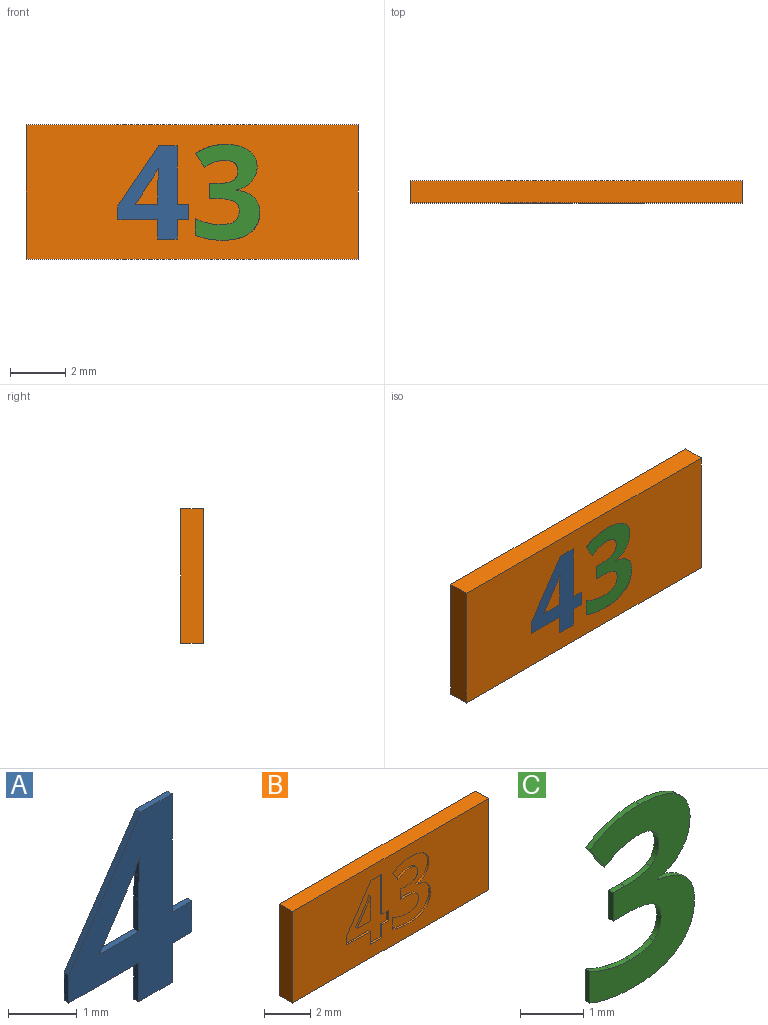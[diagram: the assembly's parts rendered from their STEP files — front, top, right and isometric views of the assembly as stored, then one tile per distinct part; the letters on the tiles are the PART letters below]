
ASSEMBLY  parts=3 mates=2
PART A: 20 faces, bbox 2.5x0.1x3.4 mm
  f0: plane 3.37x2.54mm, normal (0,-1,0), area 4.3mm2, adj f1,f2,f3,f4,f5,f6,f7,f8
  f1: plane 0.41x0.1mm, normal (0,0,1), area 0mm2, adj f0,f2,f13,f15
  f2: plane 2.12x0.1mm, normal (1,0,0), area 0.2mm2, adj f0,f1,f3,f13
  f3: plane 0.66x0.1mm, normal (0,0,1), area 0.1mm2, adj f0,f2,f4,f13
  f4: plane 2.18x1.48mm, normal (-0.83,0,0.56), area 0.3mm2, adj f0,f3,f5,f13
  f5: plane 0.5x0.1mm, normal (-1,0,0), area 0mm2, adj f0,f4,f6,f13
  f6: plane 1.44x0.1mm, normal (0,0,-1), area 0.1mm2, adj f0,f5,f7,f13
  f7: plane 0.7x0.1mm, normal (-1,0,0), area 0.1mm2, adj f0,f6,f8,f13
  f8: plane 0.7x0.1mm, normal (0,0,-1), area 0.1mm2, adj f0,f7,f13,f14
  f9: plane 0.93x0.62mm, normal (0.83,0,-0.55), area 0.1mm2, adj f0,f10,f13,f18
  f10: extruded ~0.37x0.21mm, area 0mm2, adj f0,f9,f11,f13
  f11: plane 0.1x0.02mm, normal (0,0,-1), area 0mm2, adj f0,f10,f12,f13
  f12: extruded ~0.32x0.1mm, area 0mm2, adj f0,f11,f13,f17
  f13: plane 3.37x2.54mm, normal (0,1,0), area 4.3mm2, adj f1,f2,f3,f4,f5,f6,f7,f8
  f14: plane 0.7x0.1mm, normal (1,0,0), area 0.1mm2, adj f0,f8,f13,f16
  f15: plane 0.55x0.1mm, normal (1,0,0), area 0.1mm2, adj f0,f1,f13,f16
  f16: plane 0.41x0.1mm, normal (0,0,-1), area 0mm2, adj f0,f13,f14,f15
  f17: extruded ~0.42x0.1mm, area 0mm2, adj f0,f12,f13,f19
  f18: plane 0.81x0.1mm, normal (0,0,1), area 0.1mm2, adj f0,f9,f13,f19
  f19: plane 0.57x0.1mm, normal (-1,0,0), area 0.1mm2, adj f0,f13,f17,f18
PART B: 54 faces, bbox 12x0.8x4.9 mm
  f0: plane 12x4.85mm, normal (0,-1,0), area 49.1mm2, adj f1,f2,f3,f4,f6,f7,f8,f9
  f1: plane 12x0.8mm, normal (0,0,-1), area 9.6mm2, adj f0,f2,f4,f5
  f2: plane 4.85x0.8mm, normal (1,0,0), area 3.9mm2, adj f0,f1,f3,f5
  f3: plane 12x0.8mm, normal (0,0,1), area 9.6mm2, adj f0,f2,f4,f5
  f4: plane 4.85x0.8mm, normal (-1,0,0), area 3.9mm2, adj f0,f1,f3,f5
  f5: plane 12x4.85mm, normal (0,1,0), area 58.2mm2, adj f1,f2,f3,f4
  f6: plane 0.55x0.1mm, normal (-1,0,0), area 0.1mm2, adj f0,f7,f23,f24
  f7: plane 0.41x0.1mm, normal (0,0,-1), area 0mm2, adj f0,f6,f8,f24
  f8: plane 2.12x0.1mm, normal (-1,0,0), area 0.2mm2, adj f0,f7,f9,f24
  f9: plane 0.66x0.1mm, normal (0,0,-1), area 0.1mm2, adj f0,f8,f10,f24
  f10: plane 2.18x1.48mm, normal (0.83,0,-0.56), area 0.3mm2, adj f0,f9,f11,f24
  f11: plane 0.5x0.1mm, normal (1,0,0), area 0mm2, adj f0,f10,f12,f24
  f12: plane 1.44x0.1mm, normal (0,0,1), area 0.1mm2, adj f0,f11,f13,f24
  f13: plane 0.7x0.1mm, normal (1,0,0), area 0.1mm2, adj f0,f12,f14,f24
  f14: plane 0.7x0.1mm, normal (0,0,1), area 0.1mm2, adj f0,f13,f15,f24
  f15: plane 0.7x0.1mm, normal (-1,0,0), area 0.1mm2, adj f0,f14,f23,f24
  f16: plane 0.81x0.1mm, normal (0,0,-1), area 0.1mm2, adj f17,f22,f24,f25
  f17: plane 0.93x0.62mm, normal (-0.83,0,0.55), area 0.1mm2, adj f16,f18,f24,f25
  f18: extruded ~0.37x0.21mm, area 0mm2, adj f17,f19,f24,f25
  f19: plane 0.1x0.02mm, normal (0,0,1), area 0mm2, adj f18,f20,f24,f25
  f20: extruded ~0.32x0.1mm, area 0mm2, adj f19,f21,f24,f25
  f21: extruded ~0.42x0.1mm, area 0mm2, adj f20,f22,f24,f25
  f22: plane 0.57x0.1mm, normal (1,0,0), area 0.1mm2, adj f16,f21,f24,f25
  f23: plane 0.41x0.1mm, normal (0,0,1), area 0mm2, adj f0,f6,f15,f24
  f24: plane 3.37x2.54mm, normal (0,-1,0), area 4.3mm2, adj f6,f7,f8,f9,f10,f11,f12,f13
  f25: plane 1.3x0.84mm, normal (0,-1,0), area 0.5mm2, adj f16,f17,f18,f19,f20,f21,f22
  f26: extruded ~0.59x0.3mm, area 0.1mm2, adj f0,f27,f52,f53
  f27: extruded ~0.83x0.21mm, area 0.1mm2, adj f0,f26,f28,f53
  f28: extruded ~1.1x0.33mm, area 0.1mm2, adj f0,f27,f29,f53
  f29: plane 0.49x0.33mm, normal (0.83,0,0.56), area 0.1mm2, adj f0,f28,f30,f53
  f30: extruded ~0.38x0.19mm, area 0mm2, adj f0,f29,f31,f53
  f31: extruded ~0.34x0.1mm, area 0mm2, adj f0,f30,f32,f53
  f32: extruded ~0.48x0.38mm, area 0.1mm2, adj f0,f31,f33,f53
  f33: extruded ~0.35x0.18mm, area 0mm2, adj f0,f32,f34,f53
  f34: extruded ~0.57x0.1mm, area 0.1mm2, adj f0,f33,f35,f53
  f35: plane 0.26x0.1mm, normal (0,0,-1), area 0mm2, adj f0,f34,f36,f53
  f36: plane 0.55x0.1mm, normal (1,0,0), area 0.1mm2, adj f0,f35,f37,f53
  f37: plane 0.26x0.1mm, normal (0,0,1), area 0mm2, adj f0,f36,f38,f53
  f38: extruded ~0.62x0.1mm, area 0.1mm2, adj f0,f37,f39,f53
  f39: extruded ~0.34x0.19mm, area 0mm2, adj f0,f38,f40,f53
  f40: extruded ~0.39x0.17mm, area 0mm2, adj f0,f39,f41,f53
  f41: extruded ~0.52x0.12mm, area 0.1mm2, adj f0,f40,f42,f53
  f42: extruded ~0.47x0.1mm, area 0mm2, adj f0,f41,f43,f53
  f43: extruded ~0.43x0.16mm, area 0mm2, adj f0,f42,f44,f53
  f44: plane 0.61x0.1mm, normal (1,0,0), area 0.1mm2, adj f0,f43,f45,f53
  f45: extruded ~0.97x0.18mm, area 0.1mm2, adj f0,f44,f46,f53
  f46: extruded ~1.01x0.27mm, area 0.1mm2, adj f0,f45,f47,f53
  f47: extruded ~0.76x0.35mm, area 0.1mm2, adj f0,f46,f48,f53
  f48: extruded ~0.53x0.21mm, area 0.1mm2, adj f0,f47,f49,f53
  f49: extruded ~0.62x0.25mm, area 0.1mm2, adj f0,f48,f50,f53
  f50: plane 0.1x0.01mm, normal (-1,0,0), area 0mm2, adj f0,f49,f51,f53
  f51: extruded ~0.54x0.3mm, area 0.1mm2, adj f0,f50,f52,f53
  f52: extruded ~0.54x0.19mm, area 0.1mm2, adj f0,f26,f51,f53
  f53: plane 3.47x2.33mm, normal (0,-1,0), area 4.3mm2, adj f26,f27,f28,f29,f30,f31,f32,f33
PART C: 29 faces, bbox 2.3x0.1x3.5 mm
  f0: plane 3.47x2.33mm, normal (0,-1,0), area 4.3mm2, adj f1,f2,f3,f4,f5,f6,f7,f8
  f1: extruded ~0.83x0.21mm, area 0.1mm2, adj f0,f2,f25,f27
  f2: extruded ~1.1x0.33mm, area 0.1mm2, adj f0,f1,f3,f25
  f3: plane 0.49x0.33mm, normal (-0.83,0,-0.56), area 0.1mm2, adj f0,f2,f4,f25
  f4: extruded ~0.38x0.19mm, area 0mm2, adj f0,f3,f5,f25
  f5: extruded ~0.34x0.1mm, area 0mm2, adj f0,f4,f6,f25
  f6: extruded ~0.48x0.38mm, area 0.1mm2, adj f0,f5,f7,f25
  f7: extruded ~0.35x0.18mm, area 0mm2, adj f0,f6,f8,f25
  f8: extruded ~0.57x0.1mm, area 0.1mm2, adj f0,f7,f9,f25
  f9: plane 0.26x0.1mm, normal (0,0,1), area 0mm2, adj f0,f8,f10,f25
  f10: plane 0.55x0.1mm, normal (-1,0,0), area 0.1mm2, adj f0,f9,f11,f25
  f11: plane 0.26x0.1mm, normal (0,0,-1), area 0mm2, adj f0,f10,f12,f25
  f12: extruded ~0.62x0.1mm, area 0.1mm2, adj f0,f11,f13,f25
  f13: extruded ~0.34x0.19mm, area 0mm2, adj f0,f12,f14,f25
  f14: extruded ~0.39x0.17mm, area 0mm2, adj f0,f13,f15,f25
  f15: extruded ~0.52x0.12mm, area 0.1mm2, adj f0,f14,f16,f25
  f16: extruded ~0.47x0.1mm, area 0mm2, adj f0,f15,f17,f25
  f17: extruded ~0.43x0.16mm, area 0mm2, adj f0,f16,f18,f25
  f18: plane 0.61x0.1mm, normal (-1,0,0), area 0.1mm2, adj f0,f17,f19,f25
  f19: extruded ~0.97x0.18mm, area 0.1mm2, adj f0,f18,f20,f25
  f20: extruded ~1.01x0.27mm, area 0.1mm2, adj f0,f19,f21,f25
  f21: extruded ~0.76x0.35mm, area 0.1mm2, adj f0,f20,f22,f25
  f22: extruded ~0.53x0.21mm, area 0.1mm2, adj f0,f21,f23,f25
  f23: extruded ~0.62x0.25mm, area 0.1mm2, adj f0,f22,f24,f25
  f24: plane 0.1x0.01mm, normal (1,0,0), area 0mm2, adj f0,f23,f25,f26
  f25: plane 3.47x2.33mm, normal (0,1,0), area 4.3mm2, adj f1,f2,f3,f4,f5,f6,f7,f8
  f26: extruded ~0.54x0.3mm, area 0.1mm2, adj f0,f24,f25,f28
  f27: extruded ~0.59x0.3mm, area 0.1mm2, adj f0,f1,f25,f28
  f28: extruded ~0.54x0.19mm, area 0.1mm2, adj f0,f25,f26,f27
PLACE A t=(-2.81,0.44,0.02)mm
PLACE B t=(0.05,0.44,0.02)mm
PLACE C t=(-0.17,0.44,0.02)mm
MATE fastened C.f0 <-> B.f0  axis (0,-1,0) through (0.17,-0.36,-1.54)mm
MATE fastened A.f0 <-> B.f0  axis (0,-1,0) through (-1.19,-0.36,-1.68)mm
